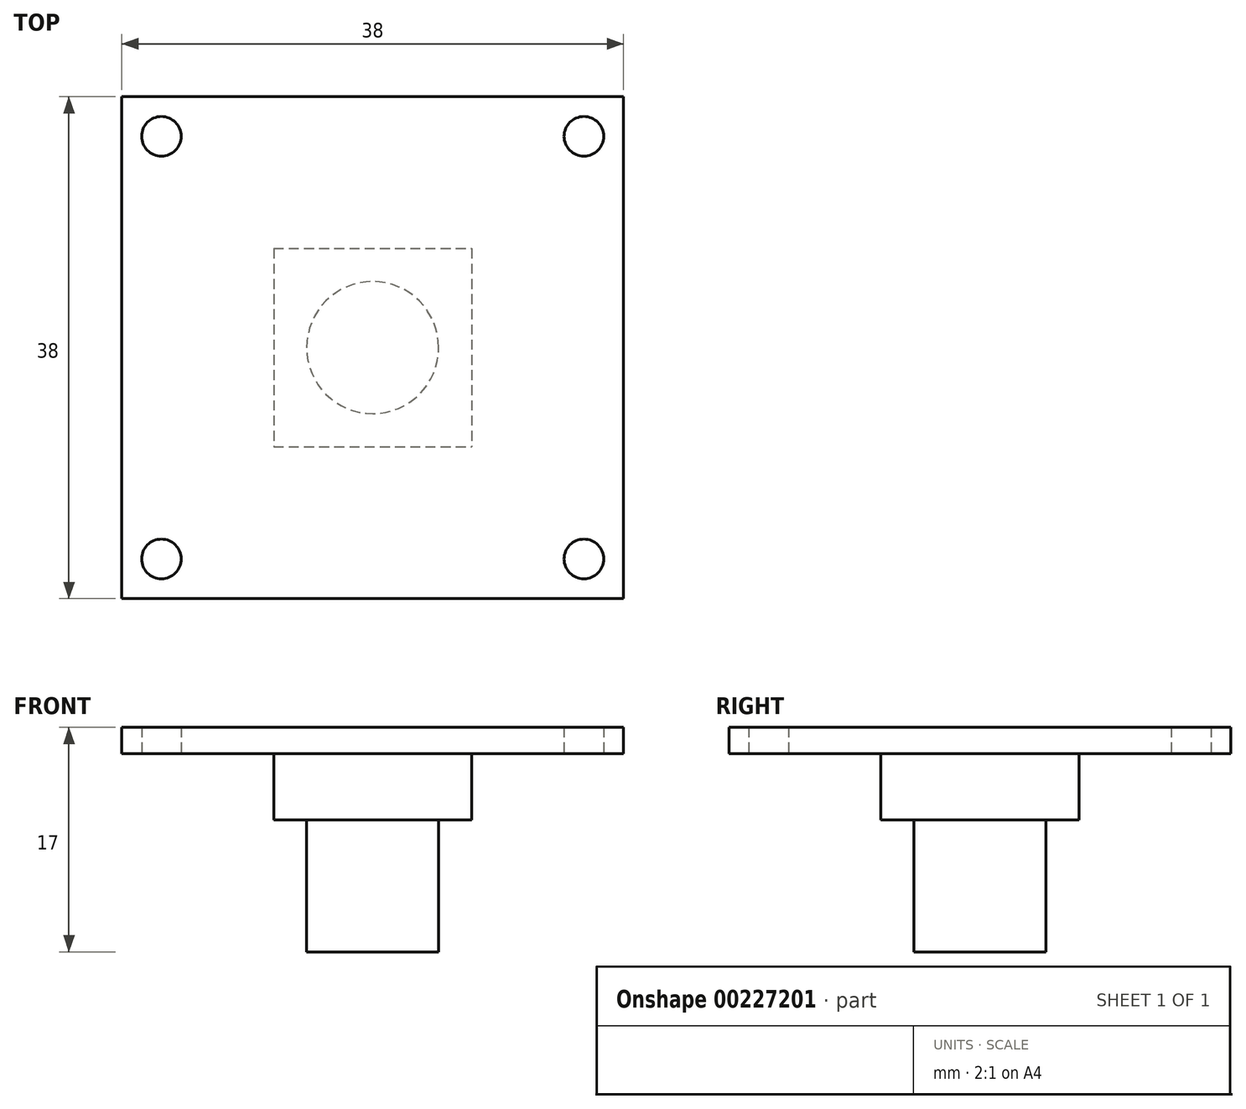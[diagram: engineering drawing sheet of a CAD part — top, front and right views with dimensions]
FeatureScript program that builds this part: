
annotation { "Feature Type Name" : "Feature", "Feature Type Description" : "" }
export const myFeature = defineFeature(function(context is Context, id is Id, definition is map)
    precondition{}
    {
        {
            var Q0;
            Q0=qCreatedBy(makeId("Top.planeOp"),FACE);
            var sketch = newSketch(context, id + "F0", { "sketchPlane" : qUnion([Q0])});
            skLineSegment(sketch, "E0.bottom", {"start": v(19, -19) * mm, "end": v(-19, -19) * mm});
            skLineSegment(sketch, "E0.top", {"start": v(19, 19) * mm, "end": v(-19, 19) * mm});
            skLineSegment(sketch, "E0.left", {"start": v(19, -19) * mm, "end": v(19, 19) * mm});
            skLineSegment(sketch, "E0.right", {"start": v(-19, -19) * mm, "end": v(-19, 19) * mm});
            skPoint(sketch, "E0.middle", {"position": v(0, 0) * mm});
            skLineSegment(sketch, "E1.bottom", {"start": v(16, -16) * mm, "end": v(-16, -16) * mm, "construction": true});
            skLineSegment(sketch, "E1.top", {"start": v(16, 16) * mm, "end": v(-16, 16) * mm, "construction": true});
            skLineSegment(sketch, "E1.left", {"start": v(16, -16) * mm, "end": v(16, 16) * mm, "construction": true});
            skLineSegment(sketch, "E1.right", {"start": v(-16, -16) * mm, "end": v(-16, 16) * mm, "construction": true});
            skCircle(sketch, "E2", {"center": v(-16, 16) * mm, "radius": 1.5 * mm});
            skCircle(sketch, "E3.1.0", {"center": v(16, 16) * mm, "radius": 1.5 * mm});
            skCircle(sketch, "E3.2.0", {"center": v(16, -16) * mm, "radius": 1.5 * mm});
            skCircle(sketch, "E3.3.0", {"center": v(-16, -16) * mm, "radius": 1.5 * mm});
            skLineSegment(sketch, "E3.anchor1", {"start": v(0, 0) * mm, "end": v(-16, 16) * mm, "construction": true});
            skLineSegment(sketch, "E3.anchor2", {"start": v(0, 0) * mm, "end": v(-16, -16) * mm, "construction": true});
            skSolve(sketch);
        }
        {
            var Q0;
            Q0=makeQuery(id+"F0.imprint","IMPRINT",FACE,{"disambiguationData":[TD([[makeQuery(id+"F0.imprint","IMPRINT",EDGE,{"derivedFrom":sQuery(id+"F0.wireOp",EDGE,"E0.bottom")}),-1.0]])]});
            extrude(context, id + "F1", {"entities" : qUnion([Q0]), "depth" : 2 * mm});
        }
        {
            var Q0;
            Q0=makeQuery(id+"F1.opExtrude","CAP_FACE",FACE,{"disambiguationData":[OSD([sQuery(id+"F0.wireOp",EDGE,"E0.bottom"),sQuery(id+"F0.wireOp",EDGE,"E0.top"),sQuery(id+"F0.wireOp",EDGE,"E0.left"),sQuery(id+"F0.wireOp",EDGE,"E0.right"),sQuery(id+"F0.wireOp",EDGE,"E2"),sQuery(id+"F0.wireOp",EDGE,"E3.1.0"),sQuery(id+"F0.wireOp",EDGE,"E3.2.0"),sQuery(id+"F0.wireOp",EDGE,"E3.3.0")])],"isStart":true});
            var sketch = newSketch(context, id + "F2", { "sketchPlane" : qUnion([Q0])});
            skLineSegment(sketch, "E4.bottom", {"start": v(-7.5, -7.5) * mm, "end": v(7.5, -7.5) * mm});
            skLineSegment(sketch, "E4.top", {"start": v(-7.5, 7.5) * mm, "end": v(7.5, 7.5) * mm});
            skLineSegment(sketch, "E4.left", {"start": v(-7.5, -7.5) * mm, "end": v(-7.5, 7.5) * mm});
            skLineSegment(sketch, "E4.right", {"start": v(7.5, -7.5) * mm, "end": v(7.5, 7.5) * mm});
            skPoint(sketch, "E4.middle", {"position": v(0, 0) * mm});
            skCircle(sketch, "E5", {"center": v(0, 0) * mm, "radius": 5 * mm});
            skSolve(sketch);
        }
        {
            var Q0;
            Q0 = qSketchRegion(id + "F2", true);
            extrude(context, id + "F3", {"entities" : qUnion([Q0]), "operationType" : NewBodyOperationType.ADD, "depth" : 5 * mm});
        }
        {
            var Q0;
            Q0=makeQuery(id+"F3.boolean.opBoolean","SPLIT",FACE,{"disambiguationData":[TD([makeQuery(id+"F3.opExtrude","SWEPT_FACE",FACE,{"disambiguationData":[OSD([sQuery(id+"F2.wireOp",EDGE,"E5")])]})])],"derivedFrom":makeQuery(id+"F1.opExtrude","CAP_FACE",FACE,{"disambiguationData":[OSD([sQuery(id+"F0.wireOp",EDGE,"E0.bottom"),sQuery(id+"F0.wireOp",EDGE,"E0.top"),sQuery(id+"F0.wireOp",EDGE,"E0.left"),sQuery(id+"F0.wireOp",EDGE,"E0.right"),sQuery(id+"F0.wireOp",EDGE,"E2"),sQuery(id+"F0.wireOp",EDGE,"E3.1.0"),sQuery(id+"F0.wireOp",EDGE,"E3.2.0"),sQuery(id+"F0.wireOp",EDGE,"E3.3.0")])],"isStart":true})});
            extrude(context, id + "F4", {"entities" : qUnion([Q0]), "operationType" : NewBodyOperationType.ADD, "depth" : 15 * mm});
        }
    });
